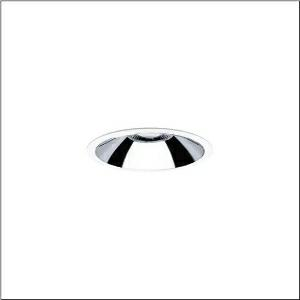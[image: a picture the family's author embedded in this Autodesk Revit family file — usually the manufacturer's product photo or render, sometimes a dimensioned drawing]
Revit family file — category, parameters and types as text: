
# Revit family: lunis_21_l_51db15dd42
name_source: partatom
category: Lighting Fixtures
units: mm (PartAtom-declared; Revit-internal decimal feet)

## family parameters
Cut with Voids When Loaded = No
Host = Face
Light Source = No
Part Type = Normal
Room Calculation Point = No
Round Connector Dimension = Use Diameter
Shared = No

## types (1)
- Lunis 21 L (1 x LED, 1700 lm, 13.8 W, 4000K)
    Apparent Load = 14 VA
    CIE Flux Codes = 90 99 100 100 100
    Color Rendering = 80
    Color Temperature = 4000K
    Default Elevation = 1800 mm
    Description = Lunis 21,  L, downlight, of PC, light emission: direct distribution, LED rated luminous flux: 1.700lm, light colour: 840, control gear: ECG DALI, with terminal, 5-pole, mains connection: 220..240V, AC, housing, round, of diecast aluminium, traffic white (RAL 9016), diameter: 162mm, protection rating (complete): IP20, insulation class (complete): insulation class II (safety insulation), certification: CE, impact resistance: IK02, packaging unit: 1 piece
    Height = 0 mm  [stored 0 ft]
    Lamp = 1 x LED
    Lamp Light Flux = 1700 lm
    Lamp Power = 13.8 W
    Lamp count = 1
    Length = 162 mm
    Luminous efficacy = 123 lm/W
    Manufacturer = Siteco
    ModVariant = No
    Model = 51DB15DD42
    Mounting Place = Ceiling
    Mounting Type = Recessed
    Number of Poles = 1
    OnlyDefault = Yes
    Power Factor = 1
    Product Name = Lunis 21 L
    Product group = downlight | ceiling recessed
    ProductGroupID = 402
    Protection Class = Protection class II
    Protection Degree = IP 20
    RLX_Detail_Level = 1
    RlxData = <blob elided: 21221 chars, md5=def9d482>
    Socket = socket
    Standby Power = 0 W
    System Light Flux = 1700 lm
    System Power = 14 W
    Type Comments = Product without accessories
    Type Image = l_1006992.jpg
    URL = http://relux.com
    VarID = ---
    Voltage = 0 V
    Weight = 0.00 kg
    Width = 0 mm  [stored 0 ft]

note: [stored X ft] marks values corroborated as IEEE doubles in the binary element streams (Revit-internal decimal feet)

## geometry (parser evidence)
native form markers: Blend x4, Sweep x13
no freeform markers — native parametric forms only
